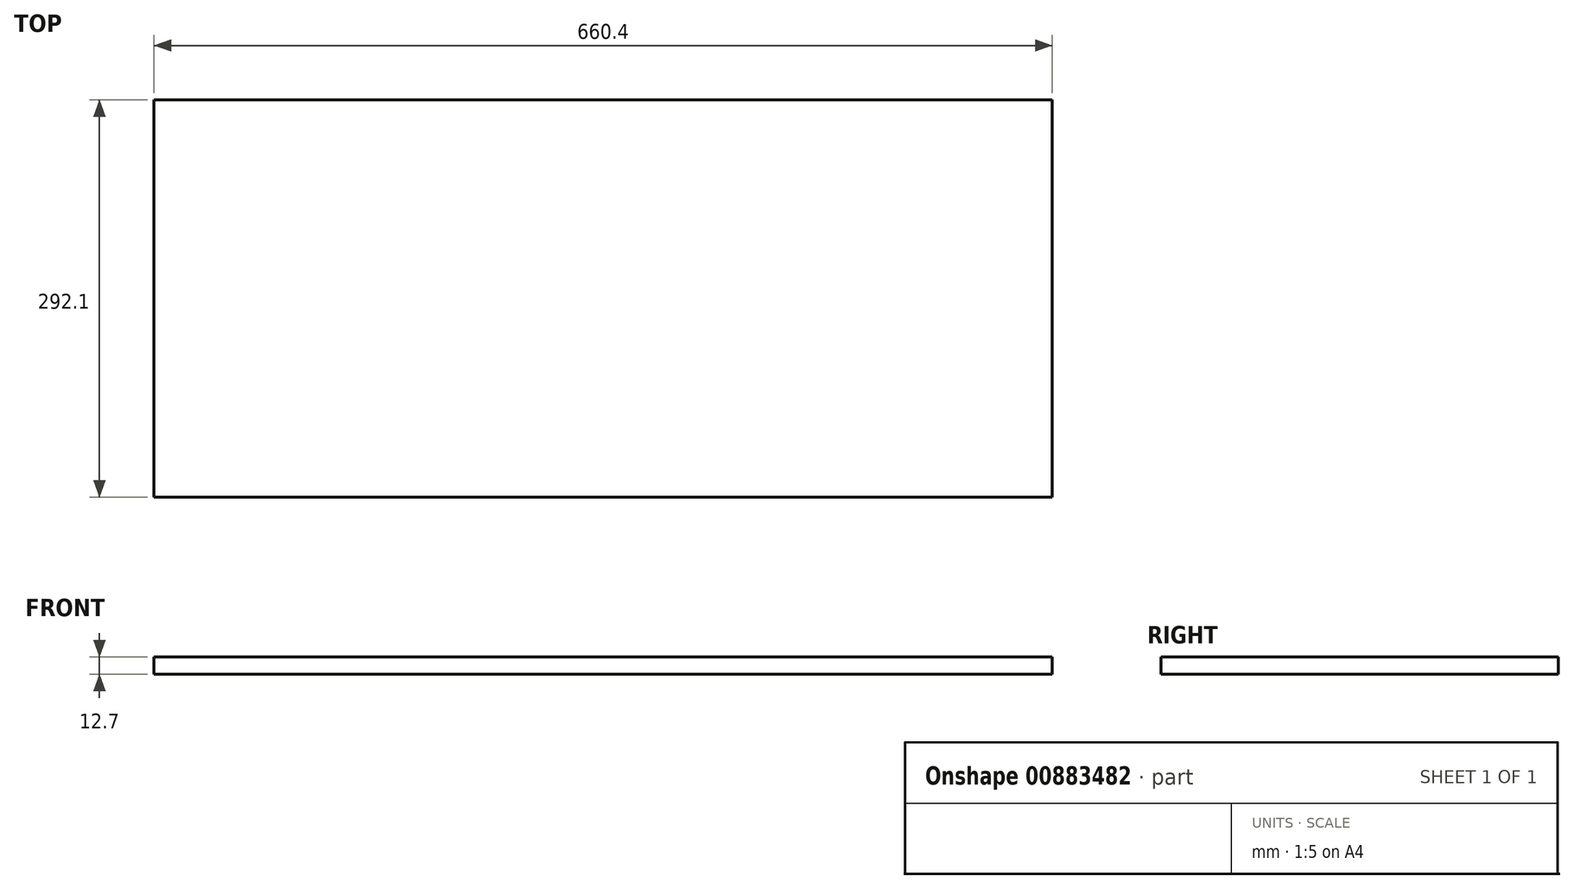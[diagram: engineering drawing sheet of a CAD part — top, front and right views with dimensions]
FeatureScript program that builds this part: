
annotation { "Feature Type Name" : "Feature", "Feature Type Description" : "" }
export const myFeature = defineFeature(function(context is Context, id is Id, definition is map)
    precondition{}
    {
        {
            var Q0;
            Q0=qCreatedBy(makeId("Top.planeOp"),FACE);
            var sketch = newSketch(context, id + "F0", { "sketchPlane" : qUnion([Q0])});
            skLineSegment(sketch, "E0.bottom", {"start": v(0, 0) * mm, "end": v(660.4, 0) * mm});
            skLineSegment(sketch, "E0.top", {"start": v(0, 292.1) * mm, "end": v(660.4, 292.1) * mm});
            skLineSegment(sketch, "E0.left", {"start": v(0, 0) * mm, "end": v(0, 292.1) * mm});
            skLineSegment(sketch, "E0.right", {"start": v(660.4, 0) * mm, "end": v(660.4, 292.1) * mm});
            skSolve(sketch);
        }
        {
            var Q0;
            Q0 = qSketchRegion(id + "F0", true);
            extrude(context, id + "F1", {"entities" : qUnion([Q0]), "depth" : 12.7 * mm, "offsetDistance" : 25.4 * mm});
        }
    });
